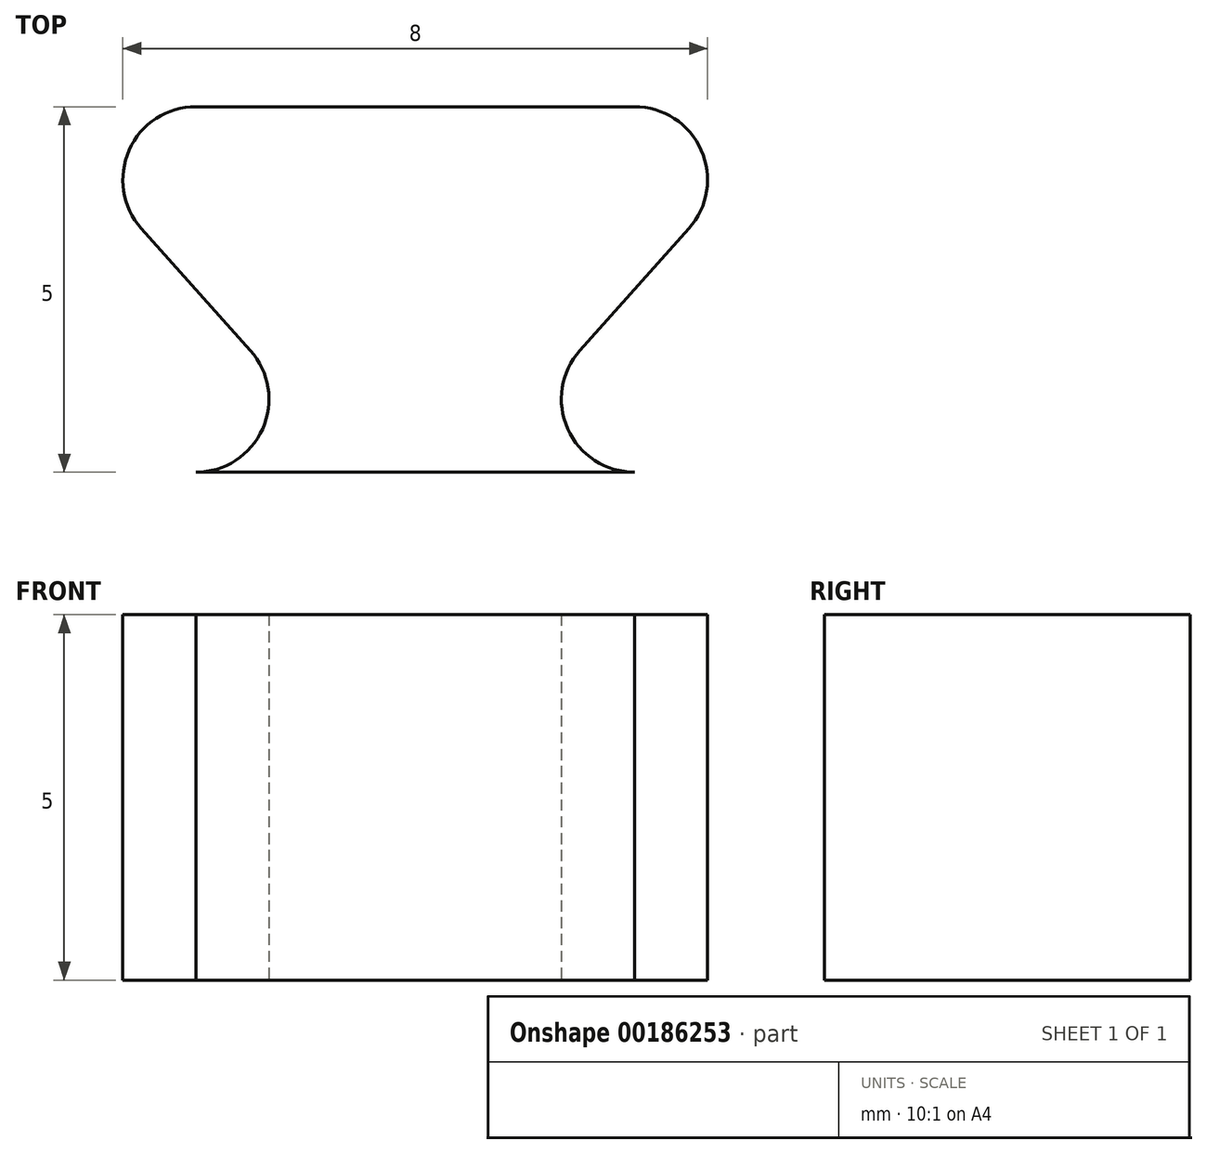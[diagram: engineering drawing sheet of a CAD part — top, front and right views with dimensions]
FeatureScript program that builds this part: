
annotation { "Feature Type Name" : "Feature", "Feature Type Description" : "" }
export const myFeature = defineFeature(function(context is Context, id is Id, definition is map)
    precondition{}
    {
        {
            var Q0;
            Q0=qCreatedBy(makeId("Top.planeOp"),FACE);
            var sketch = newSketch(context, id + "F0", { "sketchPlane" : qUnion([Q0])});
            skLineSegment(sketch, "E0", {"start": v(-3, 5) * mm, "end": v(0, 5) * mm});
            skLineSegment(sketch, "E1", {"start": v(0, 0) * mm, "end": v(-3, 0) * mm});
            skLineSegment(sketch, "E2", {"start": v(0, 0) * mm, "end": v(0, 5) * mm});
            skLineSegment(sketch, "E3", {"start": v(-2.25, 1.67) * mm, "end": v(-3.75, 3.33) * mm});
            skArc(sketch, "E4", {"start": v(-2.25, 1.67) * mm, "mid": v(-2.09, 0.6) * mm, "end": v(-3, 0) * mm});
            skArc(sketch, "E5", {"start": v(-3.75, 3.33) * mm, "mid": v(-3.91, 4.4) * mm, "end": v(-3, 5) * mm});
            skLineSegment(sketch, "E6", {"start": v(-3, 0) * mm, "end": v(-3, 5) * mm, "construction": true});
            skPoint(sketch, "E7", {"position": v(-4, 4) * mm});
            skLineSegment(sketch, "E8", {"start": v(-4, 4) * mm, "end": v(-3, 4) * mm, "construction": true});
            skSolve(sketch);
        }
        {
            var Q0;
            Q0=qSketchRegion(id+"F0",true);
            extrude(context, id + "F1", {"entities" : qUnion([Q0]), "depth" : 5 * mm});
        }
        {
            var Q0;
            Q0=makeQuery(id+"F1.opExtrude","SWEPT_BODY",BODY,{"disambiguationData":[OSD([sQuery(id+"F0.wireOp",EDGE,"E0"),sQuery(id+"F0.wireOp",EDGE,"E1"),sQuery(id+"F0.wireOp",EDGE,"E2"),sQuery(id+"F0.wireOp",EDGE,"E3"),sQuery(id+"F0.wireOp",EDGE,"E4"),sQuery(id+"F0.wireOp",EDGE,"E5")])]});
            var Q1;
            Q1=makeQuery(id+"F1.opExtrude","SWEPT_FACE",FACE,{"disambiguationData":[OSD([sQuery(id+"F0.wireOp",EDGE,"E2")])]});
            mirror(context, id + "F2", {"operationType" : NewBodyOperationType.ADD, "entities" : qUnion([Q0]), "mirrorPlane" : qUnion([Q1])});
        }
    });
